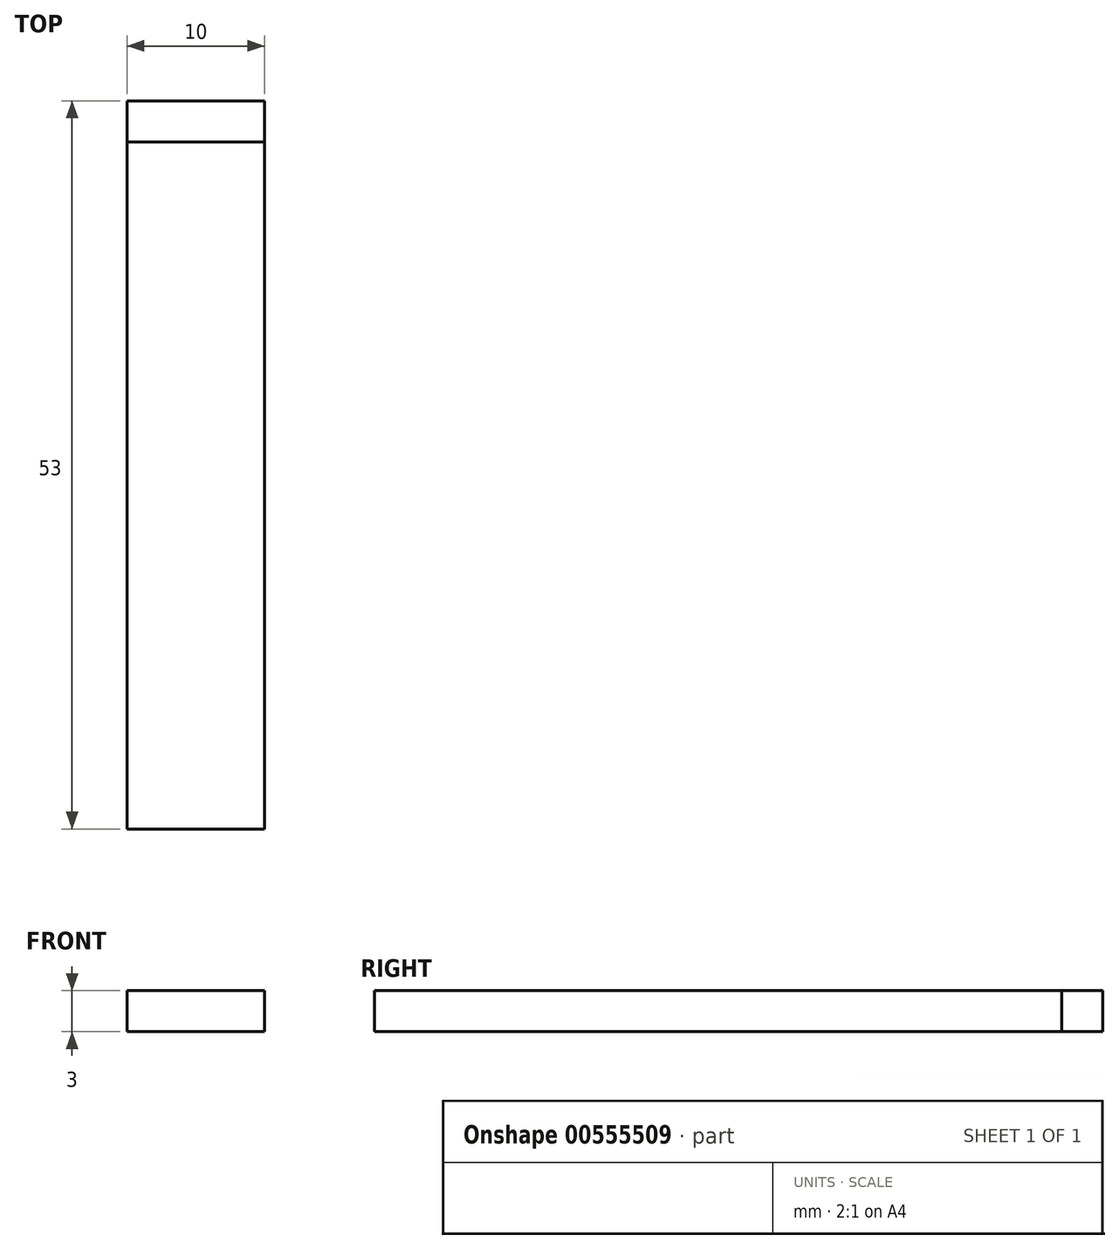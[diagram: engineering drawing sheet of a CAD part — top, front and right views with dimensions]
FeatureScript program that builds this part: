
annotation { "Feature Type Name" : "Feature", "Feature Type Description" : "" }
export const myFeature = defineFeature(function(context is Context, id is Id, definition is map)
    precondition{}
    {
        {
            var Q0;
            Q0=qCreatedBy(makeId("Front.planeOp"),FACE);
            var sketch = newSketch(context, id + "F0", { "sketchPlane" : qUnion([Q0])});
            skLineSegment(sketch, "E0.bottom", {"start": v(5, -1.5) * mm, "end": v(-5, -1.5) * mm});
            skLineSegment(sketch, "E0.top", {"start": v(5, 1.5) * mm, "end": v(-5, 1.5) * mm});
            skLineSegment(sketch, "E0.left", {"start": v(5, -1.5) * mm, "end": v(5, 1.5) * mm});
            skLineSegment(sketch, "E0.right", {"start": v(-5, -1.5) * mm, "end": v(-5, 1.5) * mm});
            skPoint(sketch, "E0.middle", {"position": v(0, 0) * mm});
            skSolve(sketch);
        }
        {
            var Q0;
            Q0 = qSketchRegion(id + "F0", true);
            extrude(context, id + "F1", {"entities" : qUnion([Q0]), "oppositeDirection" : true, "depth" : 3 * mm, "offsetDistance" : 25 * mm});
        }
        {
            var Q0;
            Q0 = qSketchRegion(id + "F0", true);
            extrude(context, id + "F2", {"entities" : qUnion([Q0]), "depth" : 50 * mm, "offsetDistance" : 25 * mm});
        }
    });
